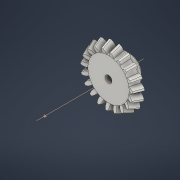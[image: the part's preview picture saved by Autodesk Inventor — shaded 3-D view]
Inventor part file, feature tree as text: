
AUTODESK INVENTOR PART (.ipt)
format: ipt  version: 2022 (Build 260153000, 153)  size: 594,944 bytes
history: native  units: mm
features: other x24, sketch x4, extrude x3, loft x2, pattern_circular x2, chamfer x1, fillet x1
ambient origin geometry x6: Origin, XZ Plane, X Axis, Y Axis, Z Axis, Center Point
bodies: Solid1 (feature_tree)
feature tree (37):
  other  "Top Point"
  other  "Mesh Plane2"
  other  "Teeth Body"
  other  "Start Point"
  other  "Tooth Plane"
  other  "Start Sketch"
  other  "End Point"
  other  "3D Sketch Right"
  other  "End Plane Right"
  loft  "Loft Right"
  pattern_circular  "Circular Pattern Right"  Angle=90.0deg  [1 undecoded]
  other  "3D Sketch Left"
  other  "End Plane Left"
  loft  "Loft Left"
  pattern_circular  "Circular Pattern Left"  [2 undecoded]
  other  "Fix Body"
  extrude  "Extrusion1"  Depth=1.5mm
  extrude  "Extrusion2"  Depth=1.5mm
  chamfer  "Chamfer1"  Distance=5.764574mm
  extrude  "Extrusion3"  Depth=1.5mm
  fillet  "Fillet1"  Radius=19.514761mm
  other  "Mesh Plane"
  other  "Top Plane"
  other  "Teeth Body Sketch"
  other  "End Plane"
  other  "End Sketch"
  other  "Helical Curve Left"
  other  "End Sketch Left"
  other  "Body Sketch"
  sketch  "Sketch6"  dims[d0=47.5mm d1=40.16154mm]
  other  "Srf1"
  other  "Helical Curve Right"
  other  "End Sketch Right"
  sketch  "Sketch8"  dims[d2=50.389413mm]
  sketch  "Sketch9"  dims[d3=8.0mm]
  sketch  "Sketch10"  dims[d4=59.428137mm d5=90.0deg d7=6.612538mm d8=8.167518mm d9=22.385367mm d11=8.275mm d12=5.764574mm d15=7.120149mm d16=19.514761mm d17=0.0mm d18=90.0deg d19=0.0mm d20=90.0deg d21=190.0mm d22=360.0deg d26=357.584802mm d27=7.69415mm d28=47.5mm d29=-3.769093mm d30=5.764574mm d31=7.120149mm d32=19.514761mm d35=0.0mm d37=0.0mm d39=0.0mm d40=90.0deg d41=190.0mm d42=360.0deg d46=90.0deg d47=90.0deg d48=0.0mm d49=0.0mm d50=90.0deg d51=1.65347mm d52=0.0mm d53=0.0mm d54=0.0mm d56=20.521955mm d57=28.746717mm d58=20.936717mm d59=25.060358mm d60=18.25188mm d61=25.060358mm d62=18.25188mm d65=357.584802mm d66=31.5mm d67=47.5mm d68=-3.769093mm d69=7.69415mm d70=7.120149mm d71=19.514761mm d72=5.764574mm d73=18.25188mm d74=25.060358mm d75=0.0mm d77=0.0mm d79=0.0mm d80=90.0deg d81=190.0mm d82=360.0deg d84=10.0mm d85=20.0mm d86=20.0mm d87=10.0mm d88=0.0mm d89=0.0mm d90=90.0deg d91=90.0deg d92=90.0deg d93=90.0deg d94=25.0mm d95=10.0mm d96=0.0mm d97=6.0mm d98=0.0mm d99=0.0mm d100=2.0mm d101=2.0mm d102=45.0deg d107=10.0mm d108=0.0mm d109=1.5mm]
  other  "Pitch Diameter"
note: 3 required parameter values undecoded (feature->parameter linkage not recoverable at this tier; creation-order binding heuristic only, values carry confidence <= 0.55)
